# Revit family: ledspotra-ava-e2_5w-dim-2700-30d-ba_541003207300
name_source: partatom
category: Leuchten
revit_build: Autodesk Revit 2016 (Build: 20190508_0715(x64)
units: mm (PartAtom-declared; Revit-internal decimal feet)

## family parameters
Basisbauteil = Fläche
Beim Laden mit Abzugskörper schneiden = Nein
Bemaßung runder Anschluss = Durchmesser verwenden
Gemeinsam genutzt = Nein
Lichtquelle = Nein
Raumberechnungspunkt = Nein
Teiletyp = Normal

## types (1)
- LEDSpotRA-Ava-E2 5W-Dim-2700-30D-BA (1 x LED, 385 lm)
    Approval mark = CE
    Beschreibung = Modern reccessed LED Spot with 25° tilting angle for perfect scene setting. Standard fully IP44, ideal for damp applications like bathrooms. Beam angle of 30° provides an accent lighting effect. Comforting warm white light tone (2700K) perfect for creating cozy ambience .
    CIE Flux Codes = 93 98 100 100 100
    Control Gear = Electronic ballast
    Height = 0 mm  [stored 0 ft]
    Hersteller = OPPLE
    Lamp Light Flux = 385 lm
    Lamp count = 1
    Lampe = 1 x LED
    Length = 85 mm
    Luminous efficacy = 77 lm/W
    ModVariant = Nein
    Modell = 541003207300
    Mounting Place = Ceiling
    Mounting Type = Recessed
    Number of Poles = 1
    OnlyDefault = Ja
    Power Factor = 1
    Product Name = LEDSpotRA-Ava-E2 5W-Dim-2700-30D-BA
    Product group = Spot Ava G2
    ProductGroupID = 425
    Protection Class = Protection class II
    Protection Degree = IP 44
    RLX_Detail_Level = 1
    RlxData = <blob elided: 185757 chars, md5=7fc3ef38>
    Scheinlast = 5 VA
    Socket = socket
    Standby Power = 0 W
    System Light Flux = 385 lm
    System Power = 5 W
    Typenbild = 541003207300.jpg
    Typenkommentare = Product without accessories
    URL = http://relux.com
    VarID = ---
    Voltage = 0 V
    Vorgabe-Ansicht = 1800 mm
    Weight = 0.00 kg
    Width = 0 mm  [stored 0 ft]

note: [stored X ft] marks values corroborated as IEEE doubles in the binary element streams (Revit-internal decimal feet)

## geometry (parser evidence)
native form markers: Blend x4, Sweep x11
no freeform markers — native parametric forms only
